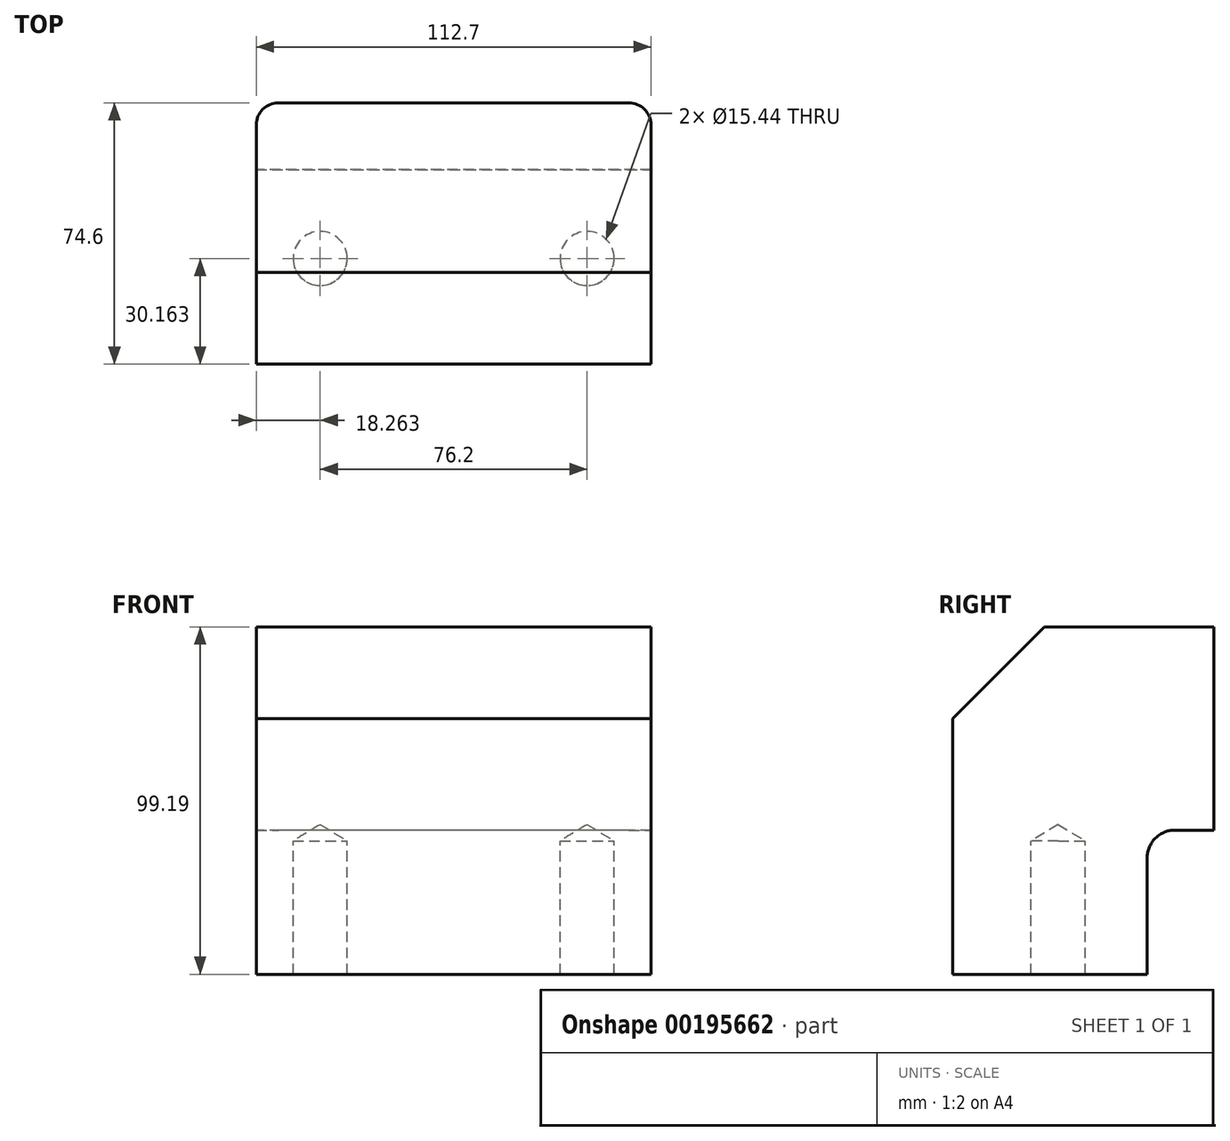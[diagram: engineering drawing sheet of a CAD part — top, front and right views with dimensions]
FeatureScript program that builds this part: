
annotation { "Feature Type Name" : "Feature", "Feature Type Description" : "" }
export const myFeature = defineFeature(function(context is Context, id is Id, definition is map)
    precondition{}
    {
        {
            var Q0;
            Q0=qCreatedBy(makeId("Right.planeOp"),FACE);
            var sketch = newSketch(context, id + "F0", { "sketchPlane" : qUnion([Q0])});
            skLineSegment(sketch, "E0", {"start": v(26.16, 99.19) * mm, "end": v(74.6, 99.19) * mm});
            skLineSegment(sketch, "E1", {"start": v(74.6, 99.19) * mm, "end": v(74.6, 41.15) * mm});
            skLineSegment(sketch, "E2", {"start": v(74.6, 41.15) * mm, "end": v(55.55, 41.15) * mm});
            skLineSegment(sketch, "E3", {"start": v(0, 0) * mm, "end": v(55.56, 0) * mm});
            skLineSegment(sketch, "E4", {"start": v(55.55, 41.15) * mm, "end": v(55.56, 0) * mm});
            skLineSegment(sketch, "E5", {"start": v(0, 0) * mm, "end": v(0, 73.03) * mm});
            skLineSegment(sketch, "E6", {"start": v(0, 73.03) * mm, "end": v(26.16, 99.19) * mm});
            skSolve(sketch);
        }
        {
            var Q0;
            Q0=makeQuery(id+"F0.imprint","IMPRINT",FACE,{"disambiguationData":[TD([[makeQuery(id+"F0.imprint","IMPRINT",EDGE,{"derivedFrom":sQuery(id+"F0.wireOp",EDGE,"E0")}),-1.0]])]});
            extrude(context, id + "F1", {"entities" : qUnion([Q0]), "depth" : 112.7 * mm});
        }
        {
            var Q0;
            Q0=makeQuery(id+"F1.opExtrude","SWEPT_FACE",FACE,{"disambiguationData":[OSD([sQuery(id+"F0.wireOp",EDGE,"E3")])]});
            var sketch = newSketch(context, id + "F2", { "sketchPlane" : qUnion([Q0])});
            skPoint(sketch, "E7", {"position": v(94.46, -30.16) * mm});
            skPoint(sketch, "E8", {"position": v(18.26, -30.16) * mm});
            skSolve(sketch);
        }
        {
            var Q0;
            Q0=sQuery(id+"F2.wireOp",VERTEX,"E7");
            var Q1;
            Q1=sQuery(id+"F2.wireOp",VERTEX,"E8");
            var Q2;
            Q2=makeQuery(id+"F1.opExtrude","SWEPT_BODY",BODY,{"disambiguationData":[OSD([sQuery(id+"F0.wireOp",EDGE,"E0"),sQuery(id+"F0.wireOp",EDGE,"E1"),sQuery(id+"F0.wireOp",EDGE,"E2"),sQuery(id+"F0.wireOp",EDGE,"E3"),sQuery(id+"F0.wireOp",EDGE,"E4"),sQuery(id+"F0.wireOp",EDGE,"E5"),sQuery(id+"F0.wireOp",EDGE,"E6")])]});
            hole(context, id + "F3", {"style" : HoleStyle.SIMPLE, "endStyle" : HoleEndStyle.BLIND, "holeDiameter" : 15.44 * mm, "holeDepth" : 38.1 * mm, "locations" : qUnion([Q0, Q1]), "scope" : qUnion([Q2])});
        }
        {
            var Q0;
            Q0=makeQuery(id+"F1.opExtrude","CAP_EDGE",EDGE,{"disambiguationData":[OSD([sQuery(id+"F0.wireOp",EDGE,"E1")])],"isStart":false});
            var Q1;
            Q1=makeQuery(id+"F1.opExtrude","CAP_EDGE",EDGE,{"disambiguationData":[OSD([sQuery(id+"F0.wireOp",EDGE,"E1")])],"isStart":true});
            fillet(context, id + "F4", {"entities" : qUnion([Q0, Q1]), "radius" : 6.35 * mm, "tangentPropagation" : true, "allowEdgeOverflow" : false});
        }
        {
            var Q0;
            Q0=makeQuery(id+"F1.opExtrude","SWEPT_EDGE",EDGE,{"disambiguationData":[OSD([sQuery(id+"F0.wireOp",EDGE,"E2"),sQuery(id+"F0.wireOp",EDGE,"E4")])]});
            fillet(context, id + "F5", {"entities" : qUnion([Q0]), "radius" : 7.94 * mm, "allowEdgeOverflow" : false});
        }
    });
